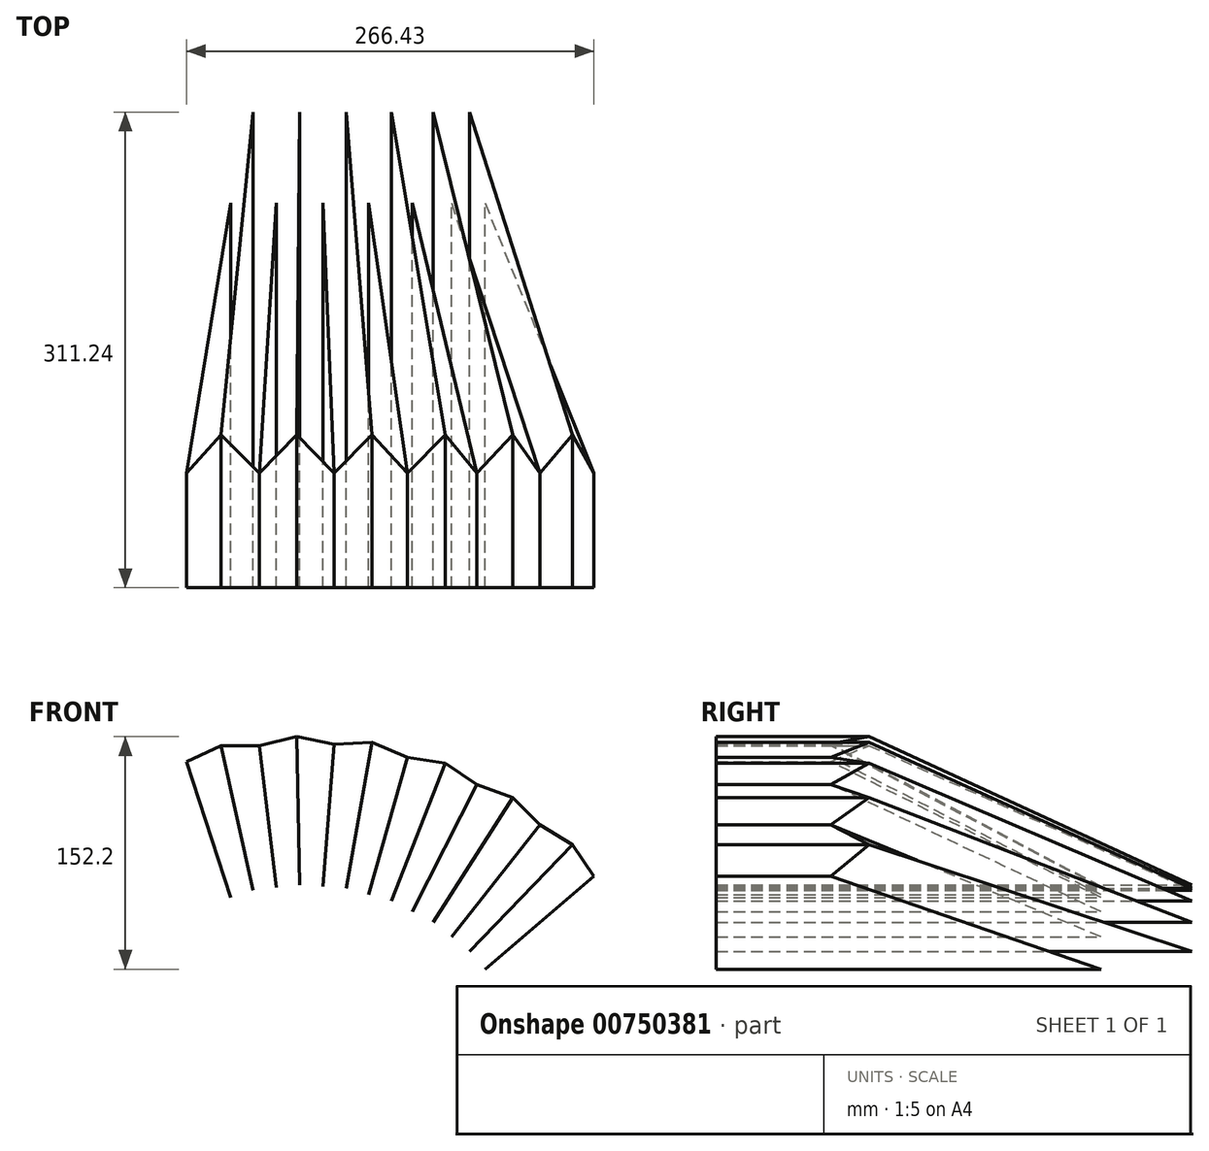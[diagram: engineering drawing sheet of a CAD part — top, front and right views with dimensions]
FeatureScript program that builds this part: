
annotation { "Feature Type Name" : "Feature", "Feature Type Description" : "" }
export const myFeature = defineFeature(function(context is Context, id is Id, definition is map)
    precondition{}
    {
        {
            assignVariable(context, id + "F0", {"name" : "w", "anyValue" : 30});
        }
        {
            assignVariable(context, id + "F1", {"name" : "v", "anyValue" : 1.5 * getVariable(context, 'w')});
        }
        {
            var Q0;
            Q0=qCreatedBy(makeId("Top.planeOp"),FACE);
            var sketch = newSketch(context, id + "F2", { "sketchPlane" : qUnion([Q0])});
            skLineSegment(sketch, "E0.bottom", {"start": v(0, 100) * mm, "end": v(25, 100) * mm, "construction": true});
            skLineSegment(sketch, "E0.top", {"start": v(0, -100) * mm, "end": v(25, -100) * mm, "construction": true});
            skLineSegment(sketch, "E0.left", {"start": v(-25, 75) * mm, "end": v(-25, -100) * mm, "construction": true});
            skLineSegment(sketch, "E0.right", {"start": v(25, 100) * mm, "end": v(25, -100) * mm});
            skPoint(sketch, "E0.middle", {"position": v(0, 0) * mm});
            skLineSegment(sketch, "E1", {"start": v(0, -100) * mm, "end": v(0, 100) * mm});
            skLineSegment(sketch, "E2", {"start": v(0, 100) * mm, "end": v(25, 75) * mm});
            skLineSegment(sketch, "E3.MirrorCS", {"start": v(0, 100) * mm, "end": v(-25, 75) * mm, "construction": true});
            skLineSegment(sketch, "E4", {"start": v(0, 0) * mm, "end": v(25, 0) * mm, "construction": true});
            skLineSegment(sketch, "E5.MirrorCS", {"start": v(0, -100) * mm, "end": v(-25, -75) * mm, "construction": true});
            skLineSegment(sketch, "E6.MirrorCS", {"start": v(0, -100) * mm, "end": v(25, -75) * mm});
            skPoint(sketch, "E7.orphan", {"position": v(-25, 100) * mm});
            skSolve(sketch);
        }
        {
            var Q0;
            Q0=sQuery(id+"F2.wireOp",EDGE,"E2");
            var Q1;
            Q1=sQuery(id+"F2.wireOp",EDGE,"E3.MirrorCS");
            cPlane(context, id + "F3", {"entities" : qUnion([Q0, Q1]), "cplaneType" : CPlaneType.LINE_ANGLE, "offset" : 25 * mm, "angle" : (getVariable(context, 'w')) * degree, "oppositeDirection" : true, "width" : 150 * mm, "height" : 150 * mm});
        }
        {
            var Q0;
            Q0=qCreatedBy(id+"F3.planeOp",FACE);
            var sketch = newSketch(context, id + "F4", { "sketchPlane" : qUnion([Q0])});
            skLineSegment(sketch, "E8", {"start": v(13.36, -69.44) * mm, "end": v(-13.36, -92.58) * mm});
            skLineSegment(sketch, "E9", {"start": v(-13.36, -92.58) * mm, "end": v(0.98, -241.9) * mm});
            skLineSegment(sketch, "E10", {"start": v(0.98, -241.9) * mm, "end": v(13.36, -69.44) * mm});
            skPoint(sketch, "E11", {"position": v(-6.2, -167.24) * mm});
            skPoint(sketch, "E12", {"position": v(0, -81) * mm});
            skLineSegment(sketch, "E13", {"start": v(0, -81) * mm, "end": v(6.43, -166.03) * mm, "construction": true});
            skLineSegment(sketch, "E14", {"start": v(6.43, -166.03) * mm, "end": v(-6.2, -167.24) * mm, "construction": true});
            skSolve(sketch);
        }
        {
            var Q0;
            Q0=sQuery(id+"F4.wireOp",EDGE,"E10");
            cPlane(context, id + "F5", {"entities" : qUnion([Q0]), "cplaneType" : CPlaneType.LINE_ANGLE, "offset" : 25 * mm, "angle" : (getVariable(context, 'v')) * degree, "oppositeDirection" : true, "width" : 150 * mm, "height" : 150 * mm});
        }
        {
            var Q0;
            Q0=qCreatedBy(id+"F5.planeOp",FACE);
            var sketch = newSketch(context, id + "F6", { "sketchPlane" : qUnion([Q0])});
            skLineSegment(sketch, "E15", {"start": v(-235.05, -54.18) * mm, "end": v(-251.2, -92.9) * mm});
            skLineSegment(sketch, "E16", {"start": v(-251.2, -92.9) * mm, "end": v(-66.22, -16.86) * mm});
            skLineSegment(sketch, "E17", {"start": v(-66.22, -16.86) * mm, "end": v(-235.05, -54.18) * mm});
            skSolve(sketch);
        }
        {
            var Q0;
            Q0=qCreatedBy(makeId("Front.planeOp"),FACE);
            var sketch = newSketch(context, id + "F7", { "sketchPlane" : qUnion([Q0])});
            skLineSegment(sketch, "E18", {"start": v(0, 0) * mm, "end": v(25, 0) * mm});
            skLineSegment(sketch, "E19", {"start": v(25, 0) * mm, "end": v(-22.7, -10.47) * mm});
            skLineSegment(sketch, "E20", {"start": v(-22.7, -10.47) * mm, "end": v(0, 0) * mm});
            skLineSegment(sketch, "E21", {"start": v(0, 0) * mm, "end": v(13.42, -61.13) * mm});
            skLineSegment(sketch, "E22", {"start": v(54.3, -247.42) * mm, "end": v(36, -92.92) * mm, "construction": true});
            skLineSegment(sketch, "E23", {"start": v(0, 0) * mm, "end": v(20.8, -94.73) * mm});
            skLineSegment(sketch, "E24", {"start": v(36, -92.92) * mm, "end": v(25, 0) * mm});
            skLineSegment(sketch, "E25", {"start": v(36, -92.92) * mm, "end": v(20.8, -94.73) * mm});
            skSolve(sketch);
        }
        {
            var Q0;
            Q0=sQuery(id+"F7.wireOp",EDGE,"E24");
            var Q1;
            Q1=qCreatedBy(id+"F5.planeOp",FACE);
            var Q2;
            Q2=sQuery(id+"F6.wireOp",VERTEX,"E16.start");
            extrude(context, id + "F8", {"bodyType" : ToolBodyType.SURFACE, "surfaceEntities" : qUnion([Q0]), "endBound" : BoundingType.UP_TO_SURFACE, "oppositeDirection" : true, "depth" : 25 * mm, "endBoundEntityFace" : qUnion([Q1]), "endBoundEntityVertex" : qUnion([Q2]), "offsetDistance" : 25 * mm});
        }
        {
            var Q0;
            Q0=sQuery(id+"F4.wireOp",VERTEX,"E10.start");
            var Q1;
            Q1=sQuery(id+"F4.wireOp",VERTEX,"E9.start");
            var Q2;
            Q2=sQuery(id+"F2.wireOp",VERTEX,"E1.start");
            cPlane(context, id + "F9", {"entities" : qUnion([Q0, Q1, Q2]), "cplaneType" : CPlaneType.THREE_POINT, "offset" : 25 * mm, "width" : 150 * mm, "height" : 150 * mm});
        }
        {
            var Q0;
            Q0=sQuery(id+"F4.wireOp",VERTEX,"E10.end");
            var Q1;
            Q1=sQuery(id+"F2.wireOp",VERTEX,"E6.MirrorCS.end");
            var Q2;
            Q2=sQuery(id+"F6.wireOp",VERTEX,"E16.start");
            cPlane(context, id + "F10", {"entities" : qUnion([Q0, Q1, Q2]), "cplaneType" : CPlaneType.THREE_POINT, "offset" : 25 * mm, "width" : 150 * mm, "height" : 150 * mm});
        }
        {
            var Q0;
            Q0=sQuery(id+"F7.wireOp",EDGE,"E23");
            var Q1;
            Q1=sQuery(id+"F7.wireOp",EDGE,"E18");
            var Q2;
            Q2=qCreatedBy(id+"F3.planeOp",FACE);
            extrude(context, id + "F11", {"bodyType" : ToolBodyType.SURFACE, "surfaceEntities" : qUnion([Q0, Q1]), "endBound" : BoundingType.UP_TO_SURFACE, "oppositeDirection" : true, "depth" : 25 * mm, "endBoundEntityFace" : qUnion([Q2]), "offsetDistance" : 25 * mm});
        }
        {
            var Q0;
            Q0=makeQuery(id+"F8.opExtrude","SWEPT_BODY",BODY,{"disambiguationData":[OSD([sQuery(id+"F7.wireOp",EDGE,"E24")])]});
            var Q1;
            Q1=makeQuery(id+"F11.opExtrude","SWEPT_BODY",BODY,{"disambiguationData":[OSD([sQuery(id+"F7.wireOp",EDGE,"E18")])]});
            var Q2;
            Q2=makeQuery(id+"F11.opExtrude","SWEPT_FACE",FACE,{"disambiguationData":[OSD([sQuery(id+"F7.wireOp",EDGE,"E23")])]});
            mirror(context, id + "F12", {"entities" : qUnion([Q0, Q1]), "mirrorPlane" : qUnion([Q2])});
        }
        {
            var Q0;
            Q0=makeQuery(id+"F12.opPattern","COPY",BODY,{"derivedFrom":makeQuery(id+"F8.opExtrude","SWEPT_BODY",BODY,{"disambiguationData":[OSD([sQuery(id+"F7.wireOp",EDGE,"E24")])]}),"instanceName":"1"});
            var Q1;
            Q1=makeQuery(id+"F11.opExtrude","SWEPT_BODY",BODY,{"disambiguationData":[OSD([sQuery(id+"F7.wireOp",EDGE,"E18")])]});
            var Q2;
            Q2=makeQuery(id+"F8.opExtrude","SWEPT_BODY",BODY,{"disambiguationData":[OSD([sQuery(id+"F7.wireOp",EDGE,"E24")])]});
            var Q3;
            Q3=makeQuery(id+"F12.opPattern","COPY",BODY,{"derivedFrom":makeQuery(id+"F11.opExtrude","SWEPT_BODY",BODY,{"disambiguationData":[OSD([sQuery(id+"F7.wireOp",EDGE,"E18")])]}),"instanceName":"1"});
            var Q4;
            Q4=makeQuery(id+"F8.opExtrude","SWEPT_FACE",FACE,{"disambiguationData":[OSD([sQuery(id+"F7.wireOp",EDGE,"E24")])]});
            mirror(context, id + "F13", {"entities" : qUnion([Q0, Q1, Q2, Q3]), "mirrorPlane" : qUnion([Q4])});
        }
        {
            var Q0;
            Q0=makeQuery(id+"F12.opPattern","COPY",BODY,{"derivedFrom":makeQuery(id+"F8.opExtrude","SWEPT_BODY",BODY,{"disambiguationData":[OSD([sQuery(id+"F7.wireOp",EDGE,"E24")])]}),"instanceName":"1"});
            var Q1;
            Q1=makeQuery(id+"F11.opExtrude","SWEPT_BODY",BODY,{"disambiguationData":[OSD([sQuery(id+"F7.wireOp",EDGE,"E18")])]});
            var Q2;
            Q2=makeQuery(id+"F12.opPattern","COPY",BODY,{"derivedFrom":makeQuery(id+"F11.opExtrude","SWEPT_BODY",BODY,{"disambiguationData":[OSD([sQuery(id+"F7.wireOp",EDGE,"E18")])]}),"instanceName":"1"});
            var Q3;
            Q3=makeQuery(id+"F13.opPattern","COPY",BODY,{"derivedFrom":makeQuery(id+"F8.opExtrude","SWEPT_BODY",BODY,{"disambiguationData":[OSD([sQuery(id+"F7.wireOp",EDGE,"E24")])]}),"instanceName":"1"});
            var Q4;
            Q4=makeQuery(id+"F13.opPattern","COPY",BODY,{"derivedFrom":makeQuery(id+"F11.opExtrude","SWEPT_BODY",BODY,{"disambiguationData":[OSD([sQuery(id+"F7.wireOp",EDGE,"E18")])]}),"instanceName":"1"});
            var Q5;
            Q5=makeQuery(id+"F13.opPattern","COPY",BODY,{"derivedFrom":makeQuery(id+"F12.opPattern","COPY",BODY,{"derivedFrom":makeQuery(id+"F11.opExtrude","SWEPT_BODY",BODY,{"disambiguationData":[OSD([sQuery(id+"F7.wireOp",EDGE,"E18")])]}),"instanceName":"1"}),"instanceName":"1"});
            var Q6;
            Q6=makeQuery(id+"F13.opPattern","COPY",BODY,{"derivedFrom":makeQuery(id+"F12.opPattern","COPY",BODY,{"derivedFrom":makeQuery(id+"F8.opExtrude","SWEPT_BODY",BODY,{"disambiguationData":[OSD([sQuery(id+"F7.wireOp",EDGE,"E24")])]}),"instanceName":"1"}),"instanceName":"1"});
            var Q7;
            Q7=makeQuery(id+"F13.opPattern","COPY",FACE,{"derivedFrom":makeQuery(id+"F12.opPattern","COPY",FACE,{"derivedFrom":makeQuery(id+"F8.opExtrude","SWEPT_FACE",FACE,{"disambiguationData":[OSD([sQuery(id+"F7.wireOp",EDGE,"E24")])]}),"instanceName":"1"}),"instanceName":"1"});
            mirror(context, id + "F14", {"entities" : qUnion([Q0, Q1, Q2, Q3, Q4, Q5, Q6]), "mirrorPlane" : qUnion([Q7])});
        }
        {
            var Q0;
            Q0=makeQuery(id+"F14.opPattern","COPY",BODY,{"derivedFrom":makeQuery(id+"F13.opPattern","COPY",BODY,{"derivedFrom":makeQuery(id+"F12.opPattern","COPY",BODY,{"derivedFrom":makeQuery(id+"F11.opExtrude","SWEPT_BODY",BODY,{"disambiguationData":[OSD([sQuery(id+"F7.wireOp",EDGE,"E18")])]}),"instanceName":"1"}),"instanceName":"1"}),"instanceName":"1"});
            var Q1;
            Q1=makeQuery(id+"F13.opPattern","COPY",BODY,{"derivedFrom":makeQuery(id+"F12.opPattern","COPY",BODY,{"derivedFrom":makeQuery(id+"F8.opExtrude","SWEPT_BODY",BODY,{"disambiguationData":[OSD([sQuery(id+"F7.wireOp",EDGE,"E24")])]}),"instanceName":"1"}),"instanceName":"1"});
            var Q2;
            Q2=makeQuery(id+"F14.opPattern","COPY",BODY,{"derivedFrom":makeQuery(id+"F13.opPattern","COPY",BODY,{"derivedFrom":makeQuery(id+"F11.opExtrude","SWEPT_BODY",BODY,{"disambiguationData":[OSD([sQuery(id+"F7.wireOp",EDGE,"E18")])]}),"instanceName":"1"}),"instanceName":"1"});
            var Q3;
            Q3=makeQuery(id+"F14.opPattern","COPY",BODY,{"derivedFrom":makeQuery(id+"F13.opPattern","COPY",BODY,{"derivedFrom":makeQuery(id+"F8.opExtrude","SWEPT_BODY",BODY,{"disambiguationData":[OSD([sQuery(id+"F7.wireOp",EDGE,"E24")])]}),"instanceName":"1"}),"instanceName":"1"});
            var Q4;
            Q4=makeQuery(id+"F14.opPattern","COPY",BODY,{"derivedFrom":makeQuery(id+"F12.opPattern","COPY",BODY,{"derivedFrom":makeQuery(id+"F11.opExtrude","SWEPT_BODY",BODY,{"disambiguationData":[OSD([sQuery(id+"F7.wireOp",EDGE,"E18")])]}),"instanceName":"1"}),"instanceName":"1"});
            var Q5;
            Q5=makeQuery(id+"F14.opPattern","COPY",BODY,{"derivedFrom":makeQuery(id+"F11.opExtrude","SWEPT_BODY",BODY,{"disambiguationData":[OSD([sQuery(id+"F7.wireOp",EDGE,"E18")])]}),"instanceName":"1"});
            var Q6;
            Q6=makeQuery(id+"F14.opPattern","COPY",FACE,{"derivedFrom":makeQuery(id+"F12.opPattern","COPY",FACE,{"derivedFrom":makeQuery(id+"F8.opExtrude","SWEPT_FACE",FACE,{"disambiguationData":[OSD([sQuery(id+"F7.wireOp",EDGE,"E24")])]}),"instanceName":"1"}),"instanceName":"1"});
            mirror(context, id + "F15", {"entities" : qUnion([Q0, Q1, Q2, Q3, Q4, Q5]), "mirrorPlane" : qUnion([Q6])});
        }
    });
